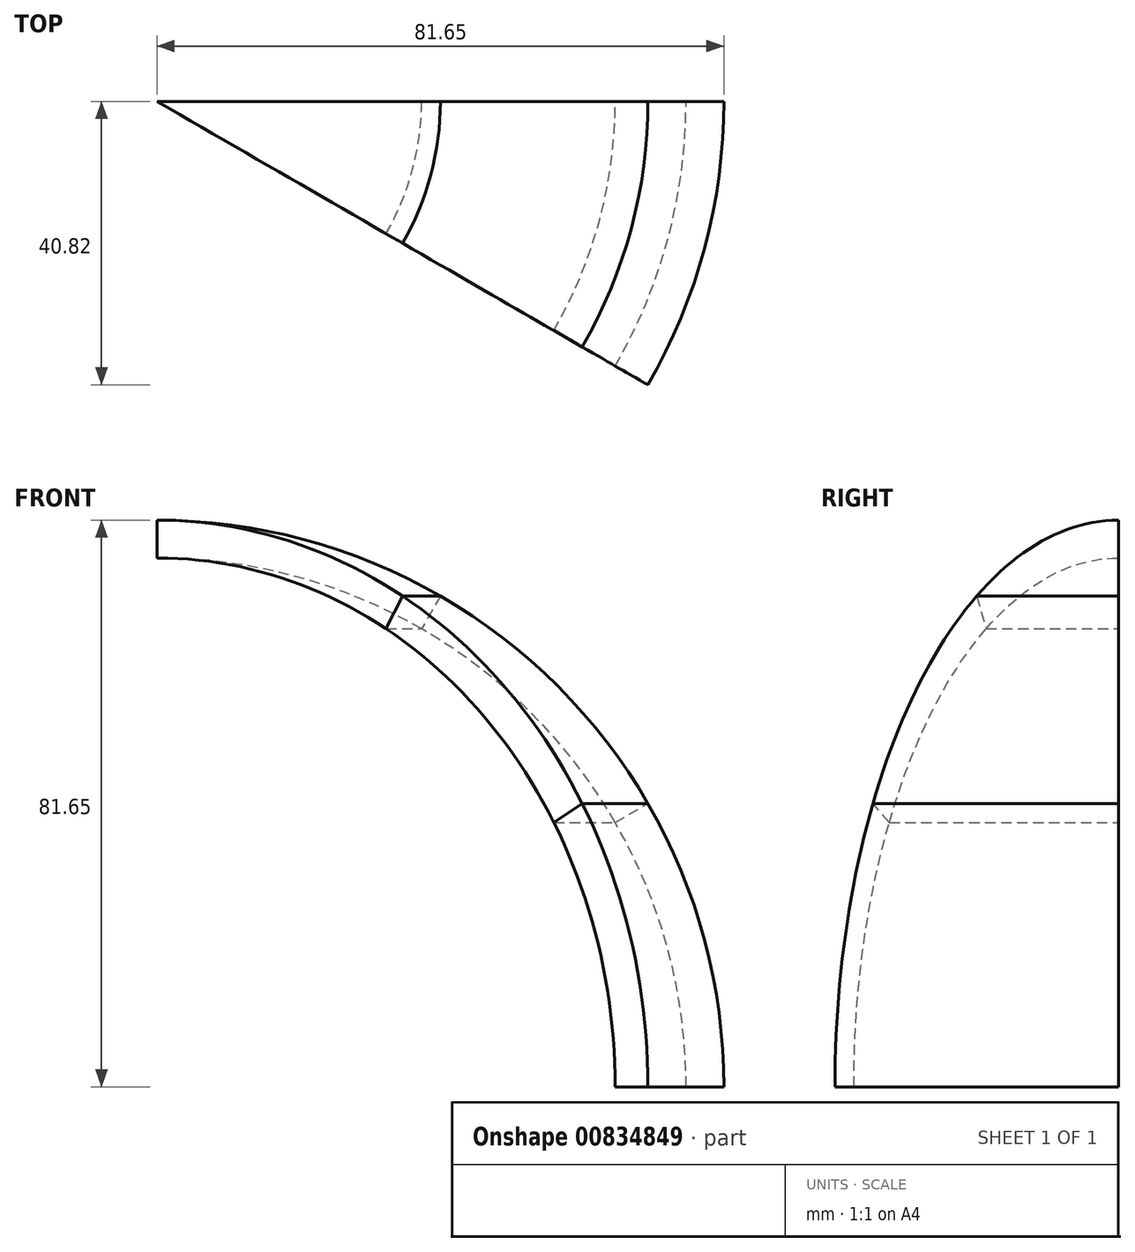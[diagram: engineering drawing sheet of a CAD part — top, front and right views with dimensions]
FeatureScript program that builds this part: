
annotation { "Feature Type Name" : "Feature", "Feature Type Description" : "" }
export const myFeature = defineFeature(function(context is Context, id is Id, definition is map)
    precondition{}
    {
        {
            var Q0;
            Q0=qCreatedBy(makeId("Front.planeOp"),FACE);
            var sketch = newSketch(context, id + "F0", { "sketchPlane" : qUnion([Q0])});
            skArc(sketch, "E0", {"start": v(76.2, 0) * mm, "mid": v(73.6, 19.72) * mm, "end": v(66, 38.1) * mm});
            skLineSegment(sketch, "E1", {"start": v(0, 0) * mm, "end": v(66, 38.1) * mm, "construction": true});
            skLineSegment(sketch, "E2", {"start": v(0, 0) * mm, "end": v(76.2, 0) * mm, "construction": true});
            skArc(sketch, "E3", {"start": v(81.65, 0) * mm, "mid": v(78.87, 21.13) * mm, "end": v(70.71, 40.82) * mm});
            skLineSegment(sketch, "E4", {"start": v(66, 38.1) * mm, "end": v(70.71, 40.82) * mm});
            skLineSegment(sketch, "E5", {"start": v(76.2, 0) * mm, "end": v(81.65, 0) * mm});
            skLineSegment(sketch, "E6", {"start": v(0, 76.2) * mm, "end": v(0, -32.64) * mm, "construction": true});
            skArc(sketch, "E7", {"start": v(70.71, 40.82) * mm, "mid": v(57.73, 57.73) * mm, "end": v(40.82, 70.71) * mm});
            skLineSegment(sketch, "E8", {"start": v(38.1, 66) * mm, "end": v(0, 0) * mm, "construction": true});
            skArc(sketch, "E9", {"start": v(40.82, 70.71) * mm, "mid": v(21.13, 78.87) * mm, "end": v(0, 81.65) * mm});
            skArc(sketch, "E10", {"start": v(66, 38.1) * mm, "mid": v(53.88, 53.88) * mm, "end": v(38.1, 66) * mm});
            skArc(sketch, "E11", {"start": v(38.1, 66) * mm, "mid": v(19.72, 73.6) * mm, "end": v(0, 76.2) * mm});
            skLineSegment(sketch, "E12", {"start": v(0, 81.65) * mm, "end": v(0, 76.2) * mm});
            skLineSegment(sketch, "E13", {"start": v(40.82, 70.71) * mm, "end": v(38.1, 66) * mm});
            skSolve(sketch);
        }
        {
            var Q0;
            Q0=makeQuery(id+"F0.imprint","IMPRINT",FACE,{"disambiguationData":[TD([[makeQuery(id+"F0.imprint","IMPRINT",EDGE,{"derivedFrom":sQuery(id+"F0.wireOp",EDGE,"E0")}),-1.0]])]});
            var Q1;
            Q1=sQuery(id+"F0.wireOp",EDGE,"E6");
            revolve(context, id + "F1", {"surfaceOperationType" : NewSurfaceOperationType.NEW, "entities" : qUnion([Q0]), "axis" : qUnion([Q1]), "revolveType" : RevolveType.ONE_DIRECTION, "angle" : 30 * degree});
        }
        {
            var Q0;
            Q0=makeQuery(id+"F0.imprint","IMPRINT",FACE,{"disambiguationData":[TD([[makeQuery(id+"F0.imprint","IMPRINT",EDGE,{"derivedFrom":sQuery(id+"F0.wireOp",EDGE,"E4")}),1.0]])]});
            var Q1;
            Q1=sQuery(id+"F0.wireOp",EDGE,"E6");
            revolve(context, id + "F2", {"surfaceOperationType" : NewSurfaceOperationType.NEW, "entities" : qUnion([Q0]), "axis" : qUnion([Q1]), "revolveType" : RevolveType.ONE_DIRECTION, "angle" : 30 * degree});
        }
        {
            var Q0;
            Q0=makeQuery(id+"F0.imprint","IMPRINT",FACE,{"disambiguationData":[TD([[makeQuery(id+"F0.imprint","IMPRINT",EDGE,{"derivedFrom":sQuery(id+"F0.wireOp",EDGE,"E9")}),1.0]])]});
            var Q1;
            Q1=sQuery(id+"F0.wireOp",EDGE,"E6");
            revolve(context, id + "F3", {"surfaceOperationType" : NewSurfaceOperationType.NEW, "entities" : qUnion([Q0]), "axis" : qUnion([Q1]), "revolveType" : RevolveType.ONE_DIRECTION, "angle" : 30 * degree});
        }
    });
